# Revit family: KKDC_TiMi_KK208_3000K_1007mm
name_source: partatom
category: 조명 설비
units: mm (PartAtom-declared; Revit-internal decimal feet)

## family parameters
OmniClass 번호 = 23.80.70.11.14.17
OmniClass 제목 = Direct/Indirect
공유 = 아니오
광원 = 예
로드될 때 보이드를 사용하여 절단 = 아니오
룸 계산 점 = 아니오
부품 유형 = 배선함
원형 커넥터 치수 = 지름 사용
작업 기준면 기반 = 예
항상 수직 = 예

## types (4) — shared parameters
Height = 6.8
Length = 1007  [stored 3.30381 ft]
Width = 9.5  [stored 0.031168 ft]
감광 램프 색상 온도 변화 = <없음>
경사도 = 90.00°
기본 입면도 = 1219.2  [stored 4 ft]
램프 = KK208
렌더링 시 발산 모양 표시 = 예
색상 필터 = 16777215
와트수 주석 = 15.6W/m
직사각형 길이에서 발산 = 1000  [stored 3.28084 ft]
직사각형 폭에서 발산 = 7  [stored 0.0229659 ft]

## per-type parameters (varying)
| type | 측광 웹 파일 |
| TiMi KK208 2100K+5000K No Cover 1007mm | TiMi No Cover.ies |
| TiMi KK208 2100K+5000K Semi-Diffused 1007mm | TiMi Semi Diffused Cover.ies |
| TiMi KK208 2100K+5000K KKLN-01 14deg 1007mm | TiMi KKLN-01 14deg.IES |
| TiMi KK208 2100K+5000K KKLN-01 36deg 1007mm | TiMi KKLN-01 36deg.IES |

note: [stored X ft] marks values corroborated as IEEE doubles in the binary element streams (Revit-internal decimal feet)
